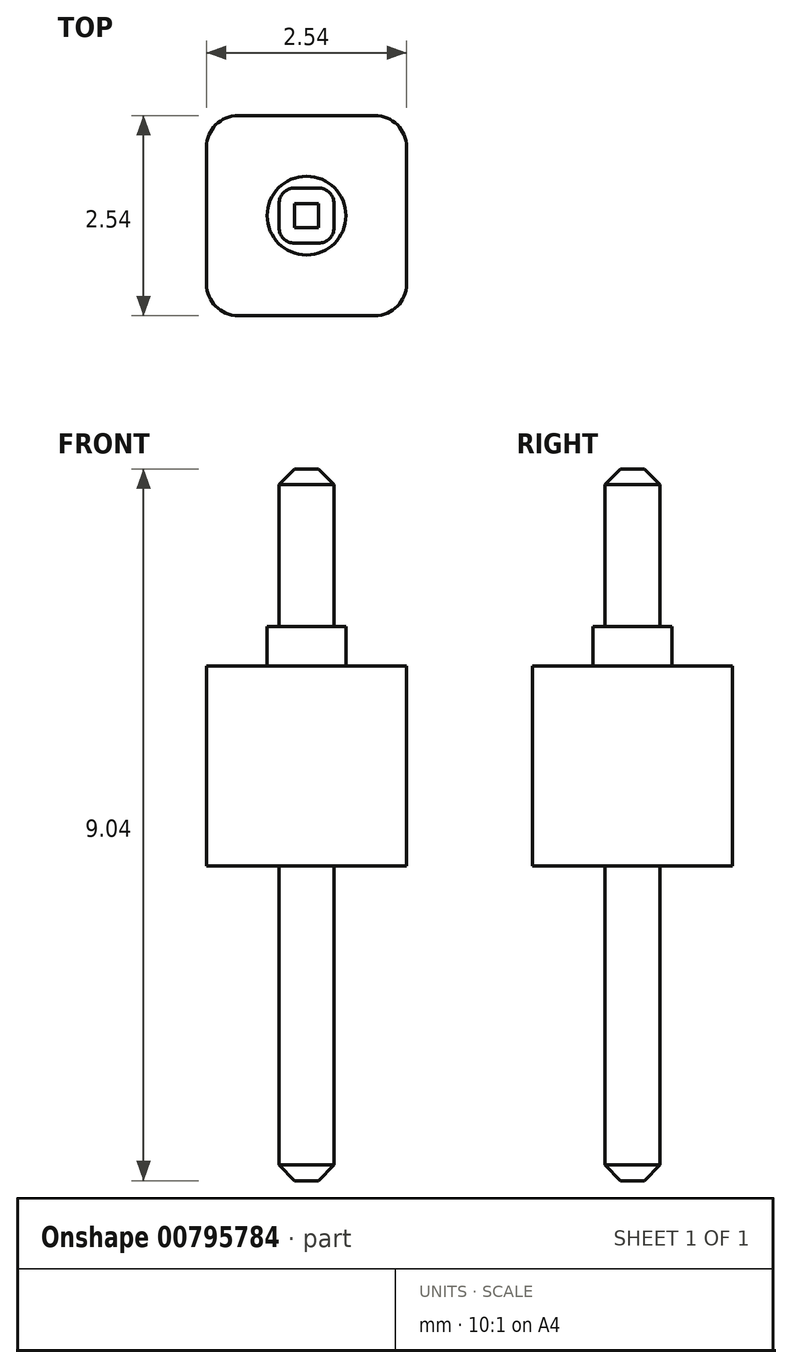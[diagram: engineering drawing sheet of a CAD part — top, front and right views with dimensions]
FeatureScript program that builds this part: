
annotation { "Feature Type Name" : "Feature", "Feature Type Description" : "" }
export const myFeature = defineFeature(function(context is Context, id is Id, definition is map)
    precondition{}
    {
        {
            var Q0;
            Q0=qCreatedBy(makeId("Top.planeOp"),FACE);
            var sketch = newSketch(context, id + "F0", { "sketchPlane" : qUnion([Q0])});
            skLineSegment(sketch, "E0.bottom", {"start": v(0.87, -1.27) * mm, "end": v(-0.87, -1.27) * mm});
            skLineSegment(sketch, "E0.top", {"start": v(0.87, 1.27) * mm, "end": v(-0.87, 1.27) * mm});
            skLineSegment(sketch, "E0.left", {"start": v(1.27, -0.87) * mm, "end": v(1.27, 0.87) * mm});
            skLineSegment(sketch, "E0.right", {"start": v(-1.27, -0.87) * mm, "end": v(-1.27, 0.87) * mm});
            skPoint(sketch, "E0.middle", {"position": v(0, 0) * mm});
            skPoint(sketch, "E1.visualSharp", {"position": v(-1.27, 1.27) * mm});
            skArc(sketch, "E1.filletArc", {"start": v(-0.87, 1.27) * mm, "mid": v(-1.15, 1.15) * mm, "end": v(-1.27, 0.87) * mm});
            skPoint(sketch, "E2.visualSharp", {"position": v(1.27, 1.27) * mm});
            skArc(sketch, "E2.filletArc", {"start": v(1.27, 0.87) * mm, "mid": v(1.15, 1.15) * mm, "end": v(0.87, 1.27) * mm});
            skPoint(sketch, "E3.visualSharp", {"position": v(-1.27, -1.27) * mm});
            skArc(sketch, "E3.filletArc", {"start": v(-1.27, -0.87) * mm, "mid": v(-1.15, -1.15) * mm, "end": v(-0.87, -1.27) * mm});
            skPoint(sketch, "E4.visualSharp", {"position": v(1.27, -1.27) * mm});
            skArc(sketch, "E4.filletArc", {"start": v(0.87, -1.27) * mm, "mid": v(1.15, -1.15) * mm, "end": v(1.27, -0.87) * mm});
            skSolve(sketch);
        }
        {
            var Q0;
            Q0=makeQuery(id+"F0.imprint","IMPRINT",FACE,{"disambiguationData":[TD([[makeQuery(id+"F0.imprint","IMPRINT",EDGE,{"derivedFrom":sQuery(id+"F0.wireOp",EDGE,"E0.bottom")}),-1.0]])]});
            extrude(context, id + "F1", {"entities" : qUnion([Q0]), "depth" : 2.54 * mm, "offsetDistance" : 25 * mm});
        }
        {
            var Q0;
            Q0=makeQuery(id+"F1.opExtrude","CAP_FACE",FACE,{"disambiguationData":[OSD([sQuery(id+"F0.wireOp",EDGE,"E0.bottom"),sQuery(id+"F0.wireOp",EDGE,"E0.top"),sQuery(id+"F0.wireOp",EDGE,"E0.left"),sQuery(id+"F0.wireOp",EDGE,"E0.right"),sQuery(id+"F0.wireOp",EDGE,"E1.filletArc"),sQuery(id+"F0.wireOp",EDGE,"E2.filletArc"),sQuery(id+"F0.wireOp",EDGE,"E3.filletArc"),sQuery(id+"F0.wireOp",EDGE,"E4.filletArc")])],"isStart":false});
            var sketch = newSketch(context, id + "F2", { "sketchPlane" : qUnion([Q0])});
            skCircle(sketch, "E5", {"center": v(0, 0) * mm, "radius": 0.5 * mm});
            skSolve(sketch);
        }
        {
            var Q0;
            Q0 = qSketchRegion(id + "F2", true);
            extrude(context, id + "F3", {"entities" : qUnion([Q0]), "operationType" : NewBodyOperationType.ADD, "depth" : 0.5 * mm, "offsetDistance" : 25 * mm});
        }
        {
            var Q0;
            Q0=makeQuery(id+"F3.opExtrude","CAP_FACE",FACE,{"disambiguationData":[OSD([sQuery(id+"F2.wireOp",EDGE,"E5")])],"isStart":false});
            var sketch = newSketch(context, id + "F4", { "sketchPlane" : qUnion([Q0])});
            skLineSegment(sketch, "E6.bottom", {"start": v(-0.15, 0.35) * mm, "end": v(0.15, 0.35) * mm});
            skLineSegment(sketch, "E6.top", {"start": v(-0.15, -0.35) * mm, "end": v(0.15, -0.35) * mm});
            skLineSegment(sketch, "E6.left", {"start": v(-0.35, 0.15) * mm, "end": v(-0.35, -0.15) * mm});
            skLineSegment(sketch, "E6.right", {"start": v(0.35, 0.15) * mm, "end": v(0.35, -0.15) * mm});
            skPoint(sketch, "E6.middle", {"position": v(0, 0) * mm});
            skPoint(sketch, "E7.visualSharp", {"position": v(0.35, -0.35) * mm});
            skArc(sketch, "E7.filletArc", {"start": v(0.15, -0.35) * mm, "mid": v(0.3, -0.3) * mm, "end": v(0.35, -0.15) * mm});
            skPoint(sketch, "E8.visualSharp", {"position": v(-0.35, -0.35) * mm});
            skArc(sketch, "E8.filletArc", {"start": v(-0.35, -0.15) * mm, "mid": v(-0.3, -0.3) * mm, "end": v(-0.15, -0.35) * mm});
            skPoint(sketch, "E9.visualSharp", {"position": v(-0.35, 0.35) * mm});
            skArc(sketch, "E9.filletArc", {"start": v(-0.15, 0.35) * mm, "mid": v(-0.3, 0.3) * mm, "end": v(-0.35, 0.15) * mm});
            skPoint(sketch, "E10.visualSharp", {"position": v(0.35, 0.35) * mm});
            skArc(sketch, "E10.filletArc", {"start": v(0.35, 0.15) * mm, "mid": v(0.3, 0.3) * mm, "end": v(0.15, 0.35) * mm});
            skSolve(sketch);
        }
        {
            var Q0;
            Q0=makeQuery(id+"F4.imprint","IMPRINT",FACE,{"disambiguationData":[TD([[makeQuery(id+"F4.imprint","IMPRINT",EDGE,{"derivedFrom":sQuery(id+"F4.wireOp",EDGE,"E6.bottom")}),-1.0]])]});
            extrude(context, id + "F5", {"entities" : qUnion([Q0]), "depth" : 2 * mm, "offsetDistance" : 25 * mm});
        }
        {
            var Q0;
            Q0=makeQuery(id+"F5.opExtrude","CAP_FACE",FACE,{"disambiguationData":[OSD([sQuery(id+"F4.wireOp",EDGE,"E6.bottom"),sQuery(id+"F4.wireOp",EDGE,"E6.top"),sQuery(id+"F4.wireOp",EDGE,"E6.left"),sQuery(id+"F4.wireOp",EDGE,"E6.right"),sQuery(id+"F4.wireOp",EDGE,"E7.filletArc"),sQuery(id+"F4.wireOp",EDGE,"E8.filletArc"),sQuery(id+"F4.wireOp",EDGE,"E9.filletArc"),sQuery(id+"F4.wireOp",EDGE,"E10.filletArc")])],"isStart":false});
            chamfer(context, id + "F6", {"entities" : qUnion([Q0]), "width" : 0.2 * mm, "tangentPropagation" : true});
        }
        {
            var Q0;
            Q0=makeQuery(id+"F1.opExtrude","CAP_FACE",FACE,{"disambiguationData":[OSD([sQuery(id+"F0.wireOp",EDGE,"E0.bottom"),sQuery(id+"F0.wireOp",EDGE,"E0.top"),sQuery(id+"F0.wireOp",EDGE,"E0.left"),sQuery(id+"F0.wireOp",EDGE,"E0.right"),sQuery(id+"F0.wireOp",EDGE,"E1.filletArc"),sQuery(id+"F0.wireOp",EDGE,"E2.filletArc"),sQuery(id+"F0.wireOp",EDGE,"E3.filletArc"),sQuery(id+"F0.wireOp",EDGE,"E4.filletArc")])],"isStart":true});
            var sketch = newSketch(context, id + "F7", { "sketchPlane" : qUnion([Q0])});
            skLineSegment(sketch, "E11.bottom", {"start": v(-0.15, -0.35) * mm, "end": v(0.15, -0.35) * mm});
            skLineSegment(sketch, "E11.top", {"start": v(-0.15, 0.35) * mm, "end": v(0.15, 0.35) * mm});
            skLineSegment(sketch, "E11.left", {"start": v(-0.35, -0.15) * mm, "end": v(-0.35, 0.15) * mm});
            skLineSegment(sketch, "E11.right", {"start": v(0.35, -0.15) * mm, "end": v(0.35, 0.15) * mm});
            skPoint(sketch, "E11.middle", {"position": v(0, 0) * mm});
            skPoint(sketch, "E11.middle.positionSnap0", {"position": v(1.27, 0) * mm});
            skPoint(sketch, "E11.middle.positionSnap1", {"position": v(0, -1.27) * mm});
            skPoint(sketch, "E11.centerSnap0", {"position": v(1.27, 0) * mm});
            skPoint(sketch, "E11.centerSnap1", {"position": v(0, -1.27) * mm});
            skPoint(sketch, "E12.visualSharp", {"position": v(0.35, 0.35) * mm});
            skArc(sketch, "E12.filletArc", {"start": v(0.35, 0.15) * mm, "mid": v(0.3, 0.3) * mm, "end": v(0.15, 0.35) * mm});
            skPoint(sketch, "E13.visualSharp", {"position": v(0.35, -0.35) * mm});
            skArc(sketch, "E13.filletArc", {"start": v(0.15, -0.35) * mm, "mid": v(0.3, -0.3) * mm, "end": v(0.35, -0.15) * mm});
            skPoint(sketch, "E14.visualSharp", {"position": v(-0.35, -0.35) * mm});
            skArc(sketch, "E14.filletArc", {"start": v(-0.35, -0.15) * mm, "mid": v(-0.3, -0.3) * mm, "end": v(-0.15, -0.35) * mm});
            skPoint(sketch, "E15.visualSharp", {"position": v(-0.35, 0.35) * mm});
            skArc(sketch, "E15.filletArc", {"start": v(-0.15, 0.35) * mm, "mid": v(-0.3, 0.3) * mm, "end": v(-0.35, 0.15) * mm});
            skSolve(sketch);
        }
        {
            var Q0;
            Q0=makeQuery(id+"F7.imprint","IMPRINT",FACE,{"disambiguationData":[TD([[makeQuery(id+"F7.imprint","IMPRINT",EDGE,{"derivedFrom":sQuery(id+"F7.wireOp",EDGE,"E11.bottom")}),1.0]])]});
            extrude(context, id + "F8", {"entities" : qUnion([Q0]), "depth" : 4 * mm, "offsetDistance" : 25 * mm});
        }
        {
            var Q0;
            Q0=makeQuery(id+"F8.opExtrude","CAP_FACE",FACE,{"disambiguationData":[OSD([sQuery(id+"F7.wireOp",EDGE,"E11.bottom"),sQuery(id+"F7.wireOp",EDGE,"E11.top"),sQuery(id+"F7.wireOp",EDGE,"E11.left"),sQuery(id+"F7.wireOp",EDGE,"E11.right"),sQuery(id+"F7.wireOp",EDGE,"E12.filletArc"),sQuery(id+"F7.wireOp",EDGE,"E13.filletArc"),sQuery(id+"F7.wireOp",EDGE,"E14.filletArc"),sQuery(id+"F7.wireOp",EDGE,"E15.filletArc")])],"isStart":false});
            chamfer(context, id + "F9", {"entities" : qUnion([Q0]), "width" : 0.2 * mm, "tangentPropagation" : true});
        }
    });
